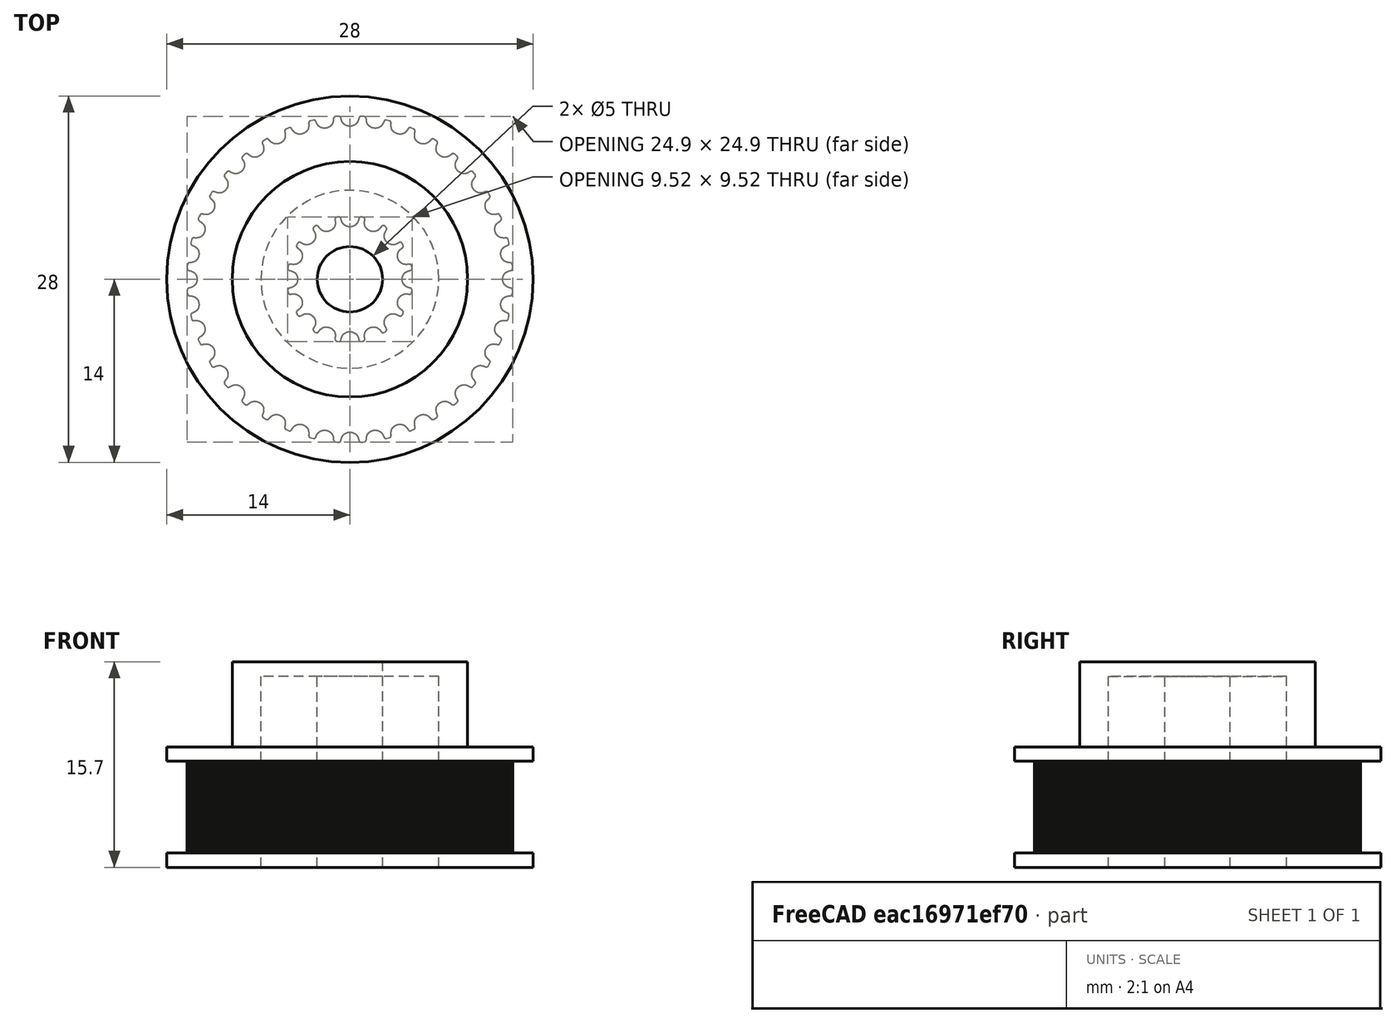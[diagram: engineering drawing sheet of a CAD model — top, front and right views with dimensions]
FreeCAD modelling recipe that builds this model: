
FCSTD DOCUMENT  (FreeCAD 0.18R16146 (Git))
Label: pulley
License: All rights reserved
LicenseURL: http://en.wikipedia.org/wiki/All_rights_reserved
objects: Part::Cylinder×7, Part::Feature×4, Part::MultiFuse×2, Part::Cut×2
note: 15 computed .brp shape members not serialized (recipe doc carries the construction recipe); baked Part::Feature solids carry a one-line shape summary decoded from their .brp

FEATURE [Part::Feature] difference001001  label="difference004"
  Placement = pos=(0,0,1.1) rot=(0,0,1;0rad)
  shape: bbox 9.529 x 9.529 x 9 mm, 374 faces (baked)
FEATURE [Part::Feature] difference003001  label="difference005"
  Placement = pos=(0,0,1.1) rot=(0,0,1;0rad)
  shape: bbox 24.9 x 24.9 x 9 mm, 902 faces (baked)
FEATURE [Part::Cylinder] Cylinder
  Angle = 360
  AttacherType = Attacher::AttachEngine3D
  Height = 1.1
  Radius = 14
FEATURE [Part::Cylinder] Cylinder001
  Angle = 360
  AttacherType = Attacher::AttachEngine3D
  Height = 1.1
  Placement = pos=(0,0,8.1) rot=(0,0,1;0rad)
  Radius = 14
FEATURE [Part::Cylinder] Cylinder002
  Angle = 360
  AttacherType = Attacher::AttachEngine3D
  Height = 6.5
  Placement = pos=(0,0,9.2) rot=(0,0,1;0rad)
  Radius = 9
FEATURE [Part::Cylinder] Cylinder003
  Angle = 360
  AttacherType = Attacher::AttachEngine3D
  Height = 20.1
  Radius = 2.5
FEATURE [Part::MultiFuse] Fusion
  Shapes = -> [Cylinder002,Cylinder001,difference003001,Cylinder]
FEATURE [Part::Cut] Cut
  Base = -> Fusion
  Tool = -> Cylinder003
FEATURE [Part::Cylinder] Cylinder004
  Angle = 360
  AttacherType = Attacher::AttachEngine3D
  Height = 1.1
  Radius = 6.8
FEATURE [Part::Cylinder] Cylinder005
  Angle = 360
  AttacherType = Attacher::AttachEngine3D
  Height = 6.5
  Placement = pos=(0,0,8.1) rot=(0,0,1;0rad)
  Radius = 6.8
FEATURE [Part::Cylinder] Cylinder006
  Angle = 360
  AttacherType = Attacher::AttachEngine3D
  Height = 21.1
  Radius = 2.5
FEATURE [Part::MultiFuse] Fusion001
  Shapes = -> [Cylinder004,difference001001,Cylinder005]
FEATURE [Part::Cut] Cut001
  Base = -> Fusion001
  Tool = -> Cylinder006
FEATURE [Part::Feature] Cut001001  label="16-teeth-pulley"
  shape: bbox 13.6 x 13.6 x 14.6 mm, 359 faces (baked)
FEATURE [Part::Feature] Cut001002  label="40-teeth^pulley"
  shape: bbox 28 x 28 x 15.7 mm, 889 faces (baked)
